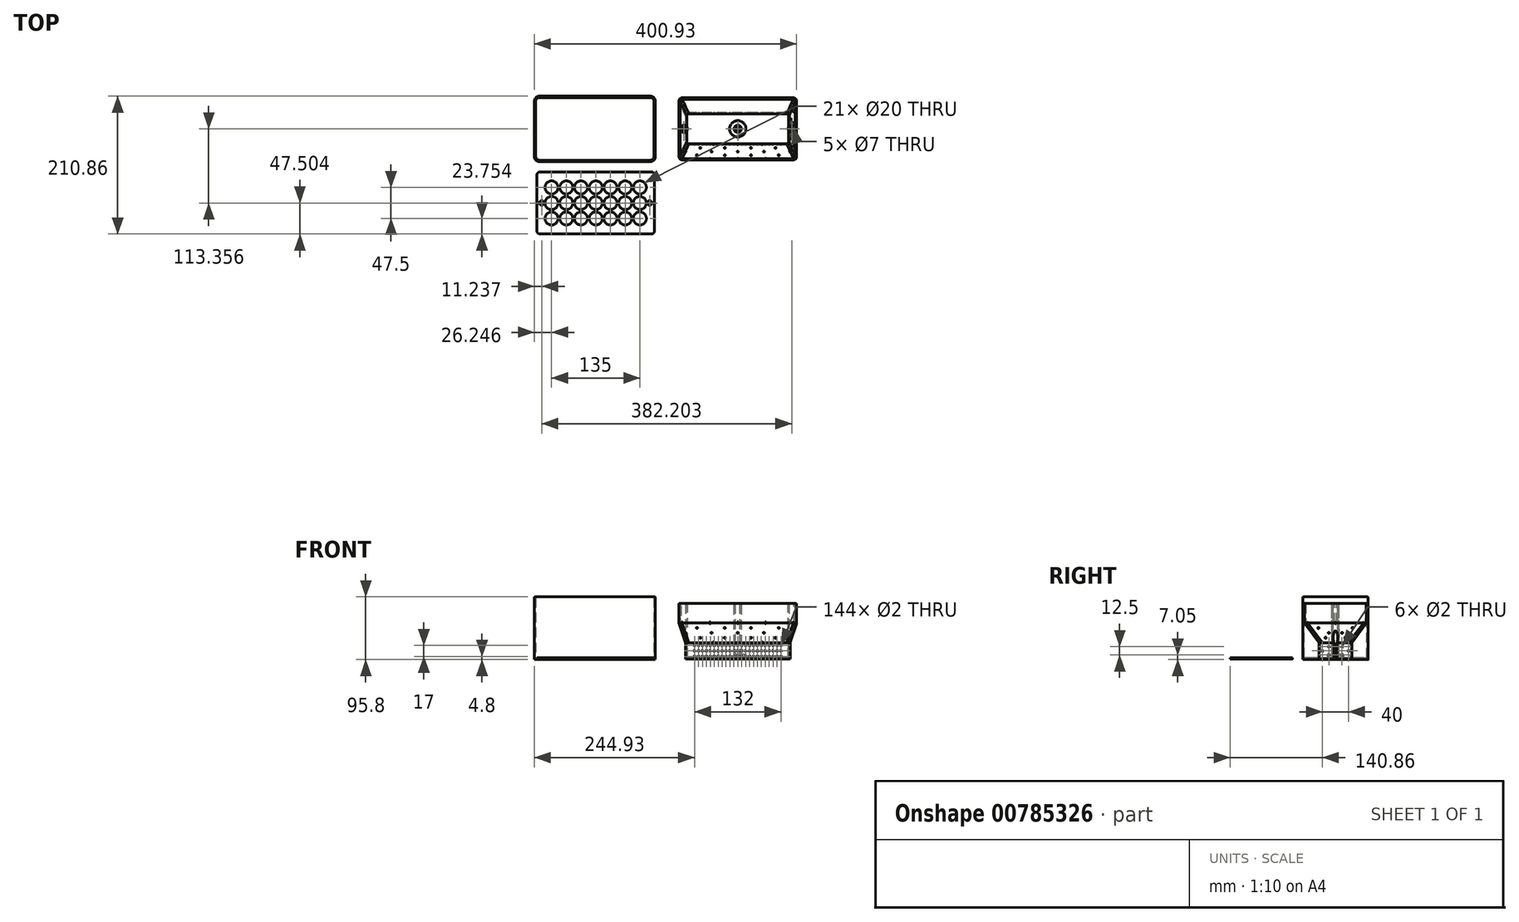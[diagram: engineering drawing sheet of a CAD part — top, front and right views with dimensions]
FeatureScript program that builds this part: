
annotation { "Feature Type Name" : "Feature", "Feature Type Description" : "" }
export const myFeature = defineFeature(function(context is Context, id is Id, definition is map)
    precondition{}
    {
        {
            var Q0;
            Q0=qCreatedBy(makeId("Top.planeOp"),FACE);
            var sketch = newSketch(context, id + "F0", { "sketchPlane" : qUnion([Q0])});
            skLineSegment(sketch, "E0.bottom", {"start": v(75, 25) * mm, "end": v(-75, 25) * mm});
            skLineSegment(sketch, "E0.top", {"start": v(75, -25) * mm, "end": v(-75, -25) * mm});
            skLineSegment(sketch, "E0.left", {"start": v(80, 20) * mm, "end": v(80, -20) * mm});
            skLineSegment(sketch, "E0.right", {"start": v(-80, 20) * mm, "end": v(-80, -20) * mm});
            skPoint(sketch, "E0.middle", {"position": v(0, 0) * mm});
            skPoint(sketch, "E1.visualSharp", {"position": v(-80, 25) * mm});
            skArc(sketch, "E1.filletArc", {"start": v(-75, 25) * mm, "mid": v(-78.54, 23.54) * mm, "end": v(-80, 20) * mm});
            skPoint(sketch, "E2.visualSharp", {"position": v(-80, -25) * mm});
            skArc(sketch, "E2.filletArc", {"start": v(-80, -20) * mm, "mid": v(-78.54, -23.54) * mm, "end": v(-75, -25) * mm});
            skPoint(sketch, "E3.visualSharp", {"position": v(80, -25) * mm});
            skArc(sketch, "E3.filletArc", {"start": v(75, -25) * mm, "mid": v(78.54, -23.54) * mm, "end": v(80, -20) * mm});
            skPoint(sketch, "E4.visualSharp", {"position": v(80, 25) * mm});
            skArc(sketch, "E4.filletArc", {"start": v(80, 20) * mm, "mid": v(78.54, 23.54) * mm, "end": v(75, 25) * mm});
            skSolve(sketch);
        }
        {
            var Q0;
            Q0 = qSketchRegion(id + "F0", true);
            extrude(context, id + "F1", {"entities" : qUnion([Q0]), "depth" : 25 * mm, "offsetDistance" : 25 * mm});
        }
        {
            var Q0;
            Q0=makeQuery(id+"F1.opExtrude","CAP_FACE",FACE,{"disambiguationData":[OSD([sQuery(id+"F0.wireOp",EDGE,"E0.bottom"),sQuery(id+"F0.wireOp",EDGE,"E0.top"),sQuery(id+"F0.wireOp",EDGE,"E0.left"),sQuery(id+"F0.wireOp",EDGE,"E0.right")])],"isStart":false});
            cPlane(context, id + "F2", {"entities" : qUnion([Q0]), "cplaneType" : CPlaneType.OFFSET, "offset" : 30 * mm, "width" : 150 * mm, "height" : 150 * mm});
        }
        {
            var Q0;
            Q0=qCreatedBy(id+"F2.planeOp",FACE);
            var sketch = newSketch(context, id + "F3", { "sketchPlane" : qUnion([Q0])});
            skLineSegment(sketch, "E5.bottom", {"start": v(85, 47.5) * mm, "end": v(-85, 47.5) * mm});
            skLineSegment(sketch, "E5.top", {"start": v(85, -47.5) * mm, "end": v(-85, -47.5) * mm});
            skLineSegment(sketch, "E5.left", {"start": v(90, 42.5) * mm, "end": v(90, -42.5) * mm});
            skLineSegment(sketch, "E5.right", {"start": v(-90, 42.5) * mm, "end": v(-90, -42.5) * mm});
            skPoint(sketch, "E5.middle", {"position": v(0, 0) * mm});
            skPoint(sketch, "E6.visualSharp", {"position": v(-90, 47.5) * mm});
            skArc(sketch, "E6.filletArc", {"start": v(-85, 47.5) * mm, "mid": v(-88.54, 46.04) * mm, "end": v(-90, 42.5) * mm});
            skPoint(sketch, "E7.visualSharp", {"position": v(-90, -47.5) * mm});
            skArc(sketch, "E7.filletArc", {"start": v(-90, -42.5) * mm, "mid": v(-88.54, -46.04) * mm, "end": v(-85, -47.5) * mm});
            skPoint(sketch, "E8.visualSharp", {"position": v(90, -47.5) * mm});
            skArc(sketch, "E8.filletArc", {"start": v(85, -47.5) * mm, "mid": v(88.54, -46.04) * mm, "end": v(90, -42.5) * mm});
            skPoint(sketch, "E9.visualSharp", {"position": v(90, 47.5) * mm});
            skArc(sketch, "E9.filletArc", {"start": v(90, 42.5) * mm, "mid": v(88.54, 46.04) * mm, "end": v(85, 47.5) * mm});
            skPoint(sketch, "E10", {"position": v(-82.5, 0) * mm});
            skPoint(sketch, "E11.MirrorP", {"position": v(82.5, 0) * mm});
            skSolve(sketch);
        }
        {
            var Q1;
            Q1=makeQuery(id+"F1.opExtrude","CAP_FACE",FACE,{"disambiguationData":[OSD([sQuery(id+"F0.wireOp",EDGE,"E0.bottom"),sQuery(id+"F0.wireOp",EDGE,"E0.top"),sQuery(id+"F0.wireOp",EDGE,"E0.left"),sQuery(id+"F0.wireOp",EDGE,"E0.right"),sQuery(id+"F0.wireOp",EDGE,"E1.filletArc"),sQuery(id+"F0.wireOp",EDGE,"E2.filletArc"),sQuery(id+"F0.wireOp",EDGE,"E3.filletArc"),sQuery(id+"F0.wireOp",EDGE,"E4.filletArc")])],"isStart":false});
            var Q2;
            Q2=makeQuery(id+"F3.imprint","IMPRINT",FACE,{"disambiguationData":[TD([[makeQuery(id+"F3.imprint","IMPRINT",EDGE,{"derivedFrom":sQuery(id+"F3.wireOp",EDGE,"E5.bottom")}),1.0]])]});
            loft(context, id + "F4", {"operationType" : NewBodyOperationType.ADD, "sheetProfilesArray" : [{ "sheetProfileEntities" : qUnion([Q1]) }, { "sheetProfileEntities" : qUnion([Q2]) }]});
        }
        {
            var Q0;
            Q0=makeQuery(id+"F3.imprint","IMPRINT",FACE,{"disambiguationData":[TD([[makeQuery(id+"F3.imprint","IMPRINT",EDGE,{"derivedFrom":sQuery(id+"F3.wireOp",EDGE,"E5.bottom")}),1.0]])]});
            extrude(context, id + "F5", {"entities" : qUnion([Q0]), "operationType" : NewBodyOperationType.ADD, "depth" : 30 * mm, "offsetDistance" : 25 * mm});
        }
        {
            var Q0;
            Q0=makeQuery(id+"F1.opExtrude","SWEPT_FACE",FACE,{"disambiguationData":[OSD([sQuery(id+"F0.wireOp",EDGE,"E0.top")])]});
            var sketch = newSketch(context, id + "F6", { "sketchPlane" : qUnion([Q0])});
            skPoint(sketch, "E12", {"position": v(-36, 12.5) * mm});
            skPoint(sketch, "E13", {"position": v(-36, 4) * mm});
            skPoint(sketch, "E14", {"position": v(-36, 21) * mm});
            skPoint(sketch, "E15", {"position": v(-30, 21) * mm});
            skPoint(sketch, "E16", {"position": v(-30, 12.5) * mm});
            skPoint(sketch, "E17", {"position": v(-30, 4) * mm});
            skPoint(sketch, "E18", {"position": v(-24, 4) * mm});
            skPoint(sketch, "E19", {"position": v(-24, 12.5) * mm});
            skPoint(sketch, "E20", {"position": v(-24, 21) * mm});
            skPoint(sketch, "E21", {"position": v(-18, 21) * mm});
            skPoint(sketch, "E22", {"position": v(-18, 12.5) * mm});
            skPoint(sketch, "E23", {"position": v(-18, 4) * mm});
            skPoint(sketch, "E24", {"position": v(-12, 4) * mm});
            skPoint(sketch, "E25", {"position": v(-12, 12.5) * mm});
            skPoint(sketch, "E26", {"position": v(-12, 21) * mm});
            skPoint(sketch, "E27", {"position": v(-6, 21) * mm});
            skPoint(sketch, "E28", {"position": v(-6, 12.5) * mm});
            skPoint(sketch, "E29", {"position": v(-6, 4) * mm});
            skPoint(sketch, "E30", {"position": v(-42, 21) * mm});
            skPoint(sketch, "E31", {"position": v(-42, 12.5) * mm});
            skPoint(sketch, "E32", {"position": v(-42, 4) * mm});
            skPoint(sketch, "E33", {"position": v(-48, 4) * mm});
            skPoint(sketch, "E34", {"position": v(-48, 12.5) * mm});
            skPoint(sketch, "E35", {"position": v(-48, 21) * mm});
            skPoint(sketch, "E36", {"position": v(-54, 21) * mm});
            skPoint(sketch, "E37", {"position": v(-54, 12.5) * mm});
            skPoint(sketch, "E38", {"position": v(-54, 4) * mm});
            skPoint(sketch, "E39", {"position": v(-60, 4) * mm});
            skPoint(sketch, "E40", {"position": v(-60, 12.5) * mm});
            skPoint(sketch, "E41", {"position": v(-60, 21) * mm});
            skPoint(sketch, "E42", {"position": v(-66, 4) * mm});
            skPoint(sketch, "E43", {"position": v(-66, 12.5) * mm});
            skPoint(sketch, "E44", {"position": v(-66, 21) * mm});
            skPoint(sketch, "E45.MirrorP", {"position": v(66, 21) * mm});
            skPoint(sketch, "E46.MirrorP", {"position": v(66, 12.5) * mm});
            skPoint(sketch, "E47.MirrorP", {"position": v(66, 4) * mm});
            skPoint(sketch, "E48.MirrorP", {"position": v(60, 4) * mm});
            skPoint(sketch, "E49.MirrorP", {"position": v(60, 12.5) * mm});
            skPoint(sketch, "E50.MirrorP", {"position": v(60, 21) * mm});
            skPoint(sketch, "E51.MirrorP", {"position": v(54, 21) * mm});
            skPoint(sketch, "E52.MirrorP", {"position": v(54, 12.5) * mm});
            skPoint(sketch, "E53.MirrorP", {"position": v(54, 4) * mm});
            skPoint(sketch, "E54.MirrorP", {"position": v(48, 4) * mm});
            skPoint(sketch, "E55.MirrorP", {"position": v(48, 12.5) * mm});
            skPoint(sketch, "E56.MirrorP", {"position": v(48, 21) * mm});
            skPoint(sketch, "E57.MirrorP", {"position": v(42, 21) * mm});
            skPoint(sketch, "E58.MirrorP", {"position": v(42, 12.5) * mm});
            skPoint(sketch, "E59.MirrorP", {"position": v(42, 4) * mm});
            skPoint(sketch, "E60.MirrorP", {"position": v(36, 4) * mm});
            skPoint(sketch, "E61.MirrorP", {"position": v(36, 12.5) * mm});
            skPoint(sketch, "E62.MirrorP", {"position": v(36, 21) * mm});
            skPoint(sketch, "E63.MirrorP", {"position": v(30, 21) * mm});
            skPoint(sketch, "E64.MirrorP", {"position": v(30, 12.5) * mm});
            skPoint(sketch, "E65.MirrorP", {"position": v(30, 4) * mm});
            skPoint(sketch, "E66.MirrorP", {"position": v(24, 4) * mm});
            skPoint(sketch, "E67.MirrorP", {"position": v(24, 12.5) * mm});
            skPoint(sketch, "E68.MirrorP", {"position": v(24, 21) * mm});
            skPoint(sketch, "E69.MirrorP", {"position": v(18, 21) * mm});
            skPoint(sketch, "E70.MirrorP", {"position": v(18, 12.5) * mm});
            skPoint(sketch, "E71.MirrorP", {"position": v(18, 4) * mm});
            skPoint(sketch, "E72.MirrorP", {"position": v(12, 4) * mm});
            skPoint(sketch, "E73.MirrorP", {"position": v(12, 12.5) * mm});
            skPoint(sketch, "E74.MirrorP", {"position": v(12, 21) * mm});
            skPoint(sketch, "E75.MirrorP", {"position": v(6, 21) * mm});
            skPoint(sketch, "E76.MirrorP", {"position": v(6, 12.5) * mm});
            skPoint(sketch, "E77.MirrorP", {"position": v(6, 4) * mm});
            skPoint(sketch, "E78", {"position": v(0, 4) * mm});
            skPoint(sketch, "E79", {"position": v(0, 12.5) * mm});
            skPoint(sketch, "E80", {"position": v(0, 21) * mm});
            skSolve(sketch);
        }
        {
            var Q0;
            Q0=makeQuery(id+"F5.opExtrude","CAP_FACE",FACE,{"disambiguationData":[OSD([sQuery(id+"F3.wireOp",EDGE,"E5.bottom"),sQuery(id+"F3.wireOp",EDGE,"E5.top"),sQuery(id+"F3.wireOp",EDGE,"E5.left"),sQuery(id+"F3.wireOp",EDGE,"E5.right"),sQuery(id+"F3.wireOp",EDGE,"E6.filletArc"),sQuery(id+"F3.wireOp",EDGE,"E7.filletArc"),sQuery(id+"F3.wireOp",EDGE,"E8.filletArc"),sQuery(id+"F3.wireOp",EDGE,"E9.filletArc")])],"isStart":false});
            var sketch = newSketch(context, id + "F7", { "sketchPlane" : qUnion([Q0])});
            skPoint(sketch, "E81", {"position": v(-82.5, 0) * mm});
            skPoint(sketch, "E82.MirrorP", {"position": v(82.5, 0) * mm});
            skPoint(sketch, "E83", {"position": v(-90, 0) * mm});
            skPoint(sketch, "E84", {"position": v(90, 0) * mm});
            skPoint(sketch, "E85", {"position": v(0, 47.5) * mm});
            skPoint(sketch, "E86", {"position": v(0, -47.5) * mm});
            skLineSegment(sketch, "E87", {"start": v(-90, 0) * mm, "end": v(90, 0) * mm});
            skLineSegment(sketch, "E88", {"start": v(0, 47.5) * mm, "end": v(0, -47.5) * mm});
            skPoint(sketch, "E89", {"position": v(0, 0) * mm});
            skPoint(sketch, "E90", {"position": v(-45, 0) * mm});
            skPoint(sketch, "E91", {"position": v(45, 0) * mm});
            skSolve(sketch);
        }
        {
            var Q0;
            Q0=sQuery(id+"F7.wireOp",VERTEX,"E81");
            var Q1;
            Q1=sQuery(id+"F7.wireOp",VERTEX,"E82.MirrorP");
            var Q2;
            Q2=makeQuery(id+"F1.opExtrude","SWEPT_BODY",BODY,{"disambiguationData":[OSD([sQuery(id+"F0.wireOp",EDGE,"E0.bottom"),sQuery(id+"F0.wireOp",EDGE,"E0.top"),sQuery(id+"F0.wireOp",EDGE,"E0.left"),sQuery(id+"F0.wireOp",EDGE,"E0.right"),sQuery(id+"F0.wireOp",EDGE,"E1.filletArc"),sQuery(id+"F0.wireOp",EDGE,"E2.filletArc"),sQuery(id+"F0.wireOp",EDGE,"E3.filletArc"),sQuery(id+"F0.wireOp",EDGE,"E4.filletArc")])]});
            hole(context, id + "F8", {"style" : HoleStyle.SIMPLE, "endStyle" : HoleEndStyle.THROUGH, "holeDiameter" : 7 * mm, "majorDiameter" : 5 * mm, "isTappedThrough" : true, "tappedDepth" : 12 * mm, "tapClearance" : 3, "locations" : qUnion([Q0, Q1]), "scope" : qUnion([Q2])});
        }
        {
            var Q0;
            Q0=sQuery(id+"F7.wireOp",VERTEX,"E89");
            var Q1;
            Q1=makeQuery(id+"F1.opExtrude","SWEPT_BODY",BODY,{"disambiguationData":[OSD([sQuery(id+"F0.wireOp",EDGE,"E0.bottom"),sQuery(id+"F0.wireOp",EDGE,"E0.top"),sQuery(id+"F0.wireOp",EDGE,"E0.left"),sQuery(id+"F0.wireOp",EDGE,"E0.right"),sQuery(id+"F0.wireOp",EDGE,"E1.filletArc"),sQuery(id+"F0.wireOp",EDGE,"E2.filletArc"),sQuery(id+"F0.wireOp",EDGE,"E3.filletArc"),sQuery(id+"F0.wireOp",EDGE,"E4.filletArc")])]});
            hole(context, id + "F9", {"style" : HoleStyle.SIMPLE, "endStyle" : HoleEndStyle.THROUGH, "holeDiameter" : 7 * mm, "majorDiameter" : 5 * mm, "isTappedThrough" : true, "tappedDepth" : 12 * mm, "tapClearance" : 3, "locations" : qUnion([Q0]), "scope" : qUnion([Q1])});
        }
        {
            var Q0;
            Q0=makeQuery(id+"F5.opExtrude","CAP_FACE",FACE,{"disambiguationData":[OSD([sQuery(id+"F3.wireOp",EDGE,"E5.bottom"),sQuery(id+"F3.wireOp",EDGE,"E5.top"),sQuery(id+"F3.wireOp",EDGE,"E5.left"),sQuery(id+"F3.wireOp",EDGE,"E5.right"),sQuery(id+"F3.wireOp",EDGE,"E6.filletArc"),sQuery(id+"F3.wireOp",EDGE,"E7.filletArc"),sQuery(id+"F3.wireOp",EDGE,"E8.filletArc"),sQuery(id+"F3.wireOp",EDGE,"E9.filletArc")])],"isStart":false});
            shell(context, id + "F10", {"entities" : qUnion([Q0]), "thickness" : 2.1 * mm});
        }
        {
            var Q0;
            Q0=sQuery(id+"F6.wireOp",VERTEX,"E44");
            var Q1;
            Q1=sQuery(id+"F6.wireOp",VERTEX,"E43");
            var Q2;
            Q2=sQuery(id+"F6.wireOp",VERTEX,"E42");
            var Q3;
            Q3=sQuery(id+"F6.wireOp",VERTEX,"E39");
            var Q4;
            Q4=sQuery(id+"F6.wireOp",VERTEX,"E40");
            var Q5;
            Q5=sQuery(id+"F6.wireOp",VERTEX,"E41");
            var Q6;
            Q6=sQuery(id+"F6.wireOp",VERTEX,"E36");
            var Q7;
            Q7=sQuery(id+"F6.wireOp",VERTEX,"E37");
            var Q8;
            Q8=sQuery(id+"F6.wireOp",VERTEX,"E38");
            var Q9;
            Q9=sQuery(id+"F6.wireOp",VERTEX,"E33");
            var Q10;
            Q10=sQuery(id+"F6.wireOp",VERTEX,"E34");
            var Q11;
            Q11=sQuery(id+"F6.wireOp",VERTEX,"E35");
            var Q12;
            Q12=sQuery(id+"F6.wireOp",VERTEX,"E30");
            var Q13;
            Q13=sQuery(id+"F6.wireOp",VERTEX,"E31");
            var Q14;
            Q14=sQuery(id+"F6.wireOp",VERTEX,"E32");
            var Q15;
            Q15=sQuery(id+"F6.wireOp",VERTEX,"E13");
            var Q16;
            Q16=sQuery(id+"F6.wireOp",VERTEX,"E12");
            var Q17;
            Q17=sQuery(id+"F6.wireOp",VERTEX,"E14");
            var Q18;
            Q18=sQuery(id+"F6.wireOp",VERTEX,"E15");
            var Q19;
            Q19=sQuery(id+"F6.wireOp",VERTEX,"E16");
            var Q20;
            Q20=sQuery(id+"F6.wireOp",VERTEX,"E17");
            var Q21;
            Q21=sQuery(id+"F6.wireOp",VERTEX,"E18");
            var Q22;
            Q22=sQuery(id+"F6.wireOp",VERTEX,"E19");
            var Q23;
            Q23=sQuery(id+"F6.wireOp",VERTEX,"E20");
            var Q24;
            Q24=sQuery(id+"F6.wireOp",VERTEX,"E21");
            var Q25;
            Q25=sQuery(id+"F6.wireOp",VERTEX,"E22");
            var Q26;
            Q26=sQuery(id+"F6.wireOp",VERTEX,"E23");
            var Q27;
            Q27=sQuery(id+"F6.wireOp",VERTEX,"E25");
            var Q28;
            Q28=sQuery(id+"F6.wireOp",VERTEX,"E24");
            var Q29;
            Q29=sQuery(id+"F6.wireOp",VERTEX,"E26");
            var Q30;
            Q30=sQuery(id+"F6.wireOp",VERTEX,"E27");
            var Q31;
            Q31=sQuery(id+"F6.wireOp",VERTEX,"E28");
            var Q32;
            Q32=sQuery(id+"F6.wireOp",VERTEX,"E29");
            var Q33;
            Q33=sQuery(id+"F6.wireOp",VERTEX,"E78");
            var Q34;
            Q34=sQuery(id+"F6.wireOp",VERTEX,"E79");
            var Q35;
            Q35=sQuery(id+"F6.wireOp",VERTEX,"E80");
            var Q36;
            Q36=sQuery(id+"F6.wireOp",VERTEX,"E75.MirrorP");
            var Q37;
            Q37=sQuery(id+"F6.wireOp",VERTEX,"E76.MirrorP");
            var Q38;
            Q38=sQuery(id+"F6.wireOp",VERTEX,"E77.MirrorP");
            var Q39;
            Q39=sQuery(id+"F6.wireOp",VERTEX,"E72.MirrorP");
            var Q40;
            Q40=sQuery(id+"F6.wireOp",VERTEX,"E73.MirrorP");
            var Q41;
            Q41=sQuery(id+"F6.wireOp",VERTEX,"E74.MirrorP");
            var Q42;
            Q42=sQuery(id+"F6.wireOp",VERTEX,"E70.MirrorP");
            var Q43;
            Q43=sQuery(id+"F6.wireOp",VERTEX,"E69.MirrorP");
            var Q44;
            Q44=sQuery(id+"F6.wireOp",VERTEX,"E71.MirrorP");
            var Q45;
            Q45=sQuery(id+"F6.wireOp",VERTEX,"E66.MirrorP");
            var Q46;
            Q46=sQuery(id+"F6.wireOp",VERTEX,"E67.MirrorP");
            var Q47;
            Q47=sQuery(id+"F6.wireOp",VERTEX,"E68.MirrorP");
            var Q48;
            Q48=sQuery(id+"F6.wireOp",VERTEX,"E63.MirrorP");
            var Q49;
            Q49=sQuery(id+"F6.wireOp",VERTEX,"E64.MirrorP");
            var Q50;
            Q50=sQuery(id+"F6.wireOp",VERTEX,"E65.MirrorP");
            var Q51;
            Q51=sQuery(id+"F6.wireOp",VERTEX,"E60.MirrorP");
            var Q52;
            Q52=sQuery(id+"F6.wireOp",VERTEX,"E61.MirrorP");
            var Q53;
            Q53=sQuery(id+"F6.wireOp",VERTEX,"E62.MirrorP");
            var Q54;
            Q54=sQuery(id+"F6.wireOp",VERTEX,"E57.MirrorP");
            var Q55;
            Q55=sQuery(id+"F6.wireOp",VERTEX,"E58.MirrorP");
            var Q56;
            Q56=sQuery(id+"F6.wireOp",VERTEX,"E59.MirrorP");
            var Q57;
            Q57=sQuery(id+"F6.wireOp",VERTEX,"E54.MirrorP");
            var Q58;
            Q58=sQuery(id+"F6.wireOp",VERTEX,"E55.MirrorP");
            var Q59;
            Q59=sQuery(id+"F6.wireOp",VERTEX,"E56.MirrorP");
            var Q60;
            Q60=sQuery(id+"F6.wireOp",VERTEX,"E51.MirrorP");
            var Q61;
            Q61=sQuery(id+"F6.wireOp",VERTEX,"E53.MirrorP");
            var Q62;
            Q62=sQuery(id+"F6.wireOp",VERTEX,"E52.MirrorP");
            var Q63;
            Q63=sQuery(id+"F6.wireOp",VERTEX,"E50.MirrorP");
            var Q64;
            Q64=sQuery(id+"F6.wireOp",VERTEX,"E49.MirrorP");
            var Q65;
            Q65=sQuery(id+"F6.wireOp",VERTEX,"E48.MirrorP");
            var Q66;
            Q66=sQuery(id+"F6.wireOp",VERTEX,"E45.MirrorP");
            var Q67;
            Q67=sQuery(id+"F6.wireOp",VERTEX,"E46.MirrorP");
            var Q68;
            Q68=sQuery(id+"F6.wireOp",VERTEX,"E47.MirrorP");
            var Q69;
            Q69=sQuery(id+"F6.wireOp",VERTEX,"2dc27312-36e5-447e-a7eb-3d5d8e6497cb");
            var Q70;
            Q70=makeQuery(id+"F1.opExtrude","SWEPT_BODY",BODY,{"disambiguationData":[OSD([sQuery(id+"F0.wireOp",EDGE,"E0.bottom"),sQuery(id+"F0.wireOp",EDGE,"E0.top"),sQuery(id+"F0.wireOp",EDGE,"E0.left"),sQuery(id+"F0.wireOp",EDGE,"E0.right"),sQuery(id+"F0.wireOp",EDGE,"E1.filletArc"),sQuery(id+"F0.wireOp",EDGE,"E2.filletArc"),sQuery(id+"F0.wireOp",EDGE,"E3.filletArc"),sQuery(id+"F0.wireOp",EDGE,"E4.filletArc")])]});
            hole(context, id + "F11", {"style" : HoleStyle.SIMPLE, "endStyle" : HoleEndStyle.THROUGH, "holeDiameter" : 2 * mm, "majorDiameter" : 5 * mm, "isTappedThrough" : true, "tappedDepth" : 12 * mm, "tapClearance" : 3, "locations" : qUnion([Q0, Q1, Q2, Q3, Q4, Q5, Q6, Q7, Q8, Q9, Q10, Q11, Q12, Q13, Q14, Q15, Q16, Q17, Q18, Q19, Q20, Q21, Q22, Q23, Q24, Q25, Q26, Q27, Q28, Q29, Q30, Q31, Q32, Q33, Q34, Q35, Q36, Q37, Q38, Q39, Q40, Q41, Q42, Q43, Q44, Q45, Q46, Q47, Q48, Q49, Q50, Q51, Q52, Q53, Q54, Q55, Q56, Q57, Q58, Q59, Q60, Q61, Q62, Q63, Q64, Q65, Q66, Q67, Q68, Q69]), "scope" : qUnion([Q70])});
        }
        {
            var Q0;
            Q0=makeQuery(id+"F4.opLoft","SWEPT_FACE",FACE,{"disambiguationData":[OSD([sQuery(id+"F0.wireOp",EDGE,"E0.top"),sQuery(id+"F0.wireOp",EDGE,"E2.filletArc"),sQuery(id+"F0.wireOp",EDGE,"E3.filletArc"),sQuery(id+"F3.wireOp",EDGE,"E5.top"),sQuery(id+"F3.wireOp",EDGE,"E7.filletArc"),sQuery(id+"F3.wireOp",EDGE,"E8.filletArc")])]});
            var sketch = newSketch(context, id + "F12", { "sketchPlane" : qUnion([Q0])});
            skPoint(sketch, "E92", {"position": v(0, 35) * mm});
            skPoint(sketch, "E93", {"position": v(0, 72.5) * mm});
            skPoint(sketch, "E94", {"position": v(-75, 35) * mm});
            skPoint(sketch, "E95", {"position": v(75, 35) * mm});
            skPoint(sketch, "E96", {"position": v(85, 72.5) * mm});
            skPoint(sketch, "E97", {"position": v(-85, 72.5) * mm});
            skPoint(sketch, "E98", {"position": v(0, 53.75) * mm});
            skPoint(sketch, "E99", {"position": v(-37.5, 35) * mm});
            skPoint(sketch, "E100", {"position": v(-42.5, 72.5) * mm});
            skPoint(sketch, "E101", {"position": v(42.5, 72.5) * mm});
            skPoint(sketch, "E102", {"position": v(37.5, 35) * mm});
            skPoint(sketch, "E103", {"position": v(-80, 53.75) * mm});
            skPoint(sketch, "E104", {"position": v(80, 53.75) * mm});
            skPoint(sketch, "E105", {"position": v(-40, 53.75) * mm});
            skPoint(sketch, "E106", {"position": v(40, 53.75) * mm});
            skPoint(sketch, "E107", {"position": v(-57.5, 44.38) * mm});
            skPoint(sketch, "E108", {"position": v(-62.5, 63.12) * mm});
            skPoint(sketch, "E109", {"position": v(-20, 63.12) * mm});
            skPoint(sketch, "E110", {"position": v(-20, 44.37) * mm});
            skPoint(sketch, "E111", {"position": v(20, 44.38) * mm});
            skPoint(sketch, "E112", {"position": v(20, 63.12) * mm});
            skPoint(sketch, "E113", {"position": v(62.5, 63.12) * mm});
            skPoint(sketch, "E114", {"position": v(57.5, 44.38) * mm});
            skSolve(sketch);
        }
        {
            var Q0;
            Q0=sQuery(id+"F12.wireOp",VERTEX,"E97");
            var Q1;
            Q1=sQuery(id+"F12.wireOp",VERTEX,"E103");
            var Q2;
            Q2=sQuery(id+"F12.wireOp",VERTEX,"E94");
            var Q3;
            Q3=sQuery(id+"F12.wireOp",VERTEX,"E107");
            var Q4;
            Q4=sQuery(id+"F12.wireOp",VERTEX,"E105");
            var Q5;
            Q5=sQuery(id+"F12.wireOp",VERTEX,"E109");
            var Q6;
            Q6=sQuery(id+"F12.wireOp",VERTEX,"E93");
            var Q7;
            Q7=sQuery(id+"F12.wireOp",VERTEX,"E100");
            var Q8;
            Q8=sQuery(id+"F12.wireOp",VERTEX,"E99");
            var Q9;
            Q9=sQuery(id+"F12.wireOp",VERTEX,"E110");
            var Q10;
            Q10=sQuery(id+"F12.wireOp",VERTEX,"E98");
            var Q11;
            Q11=sQuery(id+"F12.wireOp",VERTEX,"E92");
            var Q12;
            Q12=sQuery(id+"F12.wireOp",VERTEX,"E111");
            var Q13;
            Q13=sQuery(id+"F12.wireOp",VERTEX,"E106");
            var Q14;
            Q14=sQuery(id+"F12.wireOp",VERTEX,"E113");
            var Q15;
            Q15=sQuery(id+"F12.wireOp",VERTEX,"E96");
            var Q16;
            Q16=sQuery(id+"F12.wireOp",VERTEX,"E104");
            var Q17;
            Q17=sQuery(id+"F12.wireOp",VERTEX,"E101");
            var Q18;
            Q18=sQuery(id+"F12.wireOp",VERTEX,"E112");
            var Q19;
            Q19=sQuery(id+"F12.wireOp",VERTEX,"E114");
            var Q20;
            Q20=sQuery(id+"F12.wireOp",VERTEX,"E95");
            var Q21;
            Q21=sQuery(id+"F12.wireOp",VERTEX,"E102");
            var Q22;
            Q22=sQuery(id+"F12.wireOp",VERTEX,"E108");
            var Q23;
            Q23=makeQuery(id+"F1.opExtrude","SWEPT_BODY",BODY,{"disambiguationData":[OSD([sQuery(id+"F0.wireOp",EDGE,"E0.bottom"),sQuery(id+"F0.wireOp",EDGE,"E0.top"),sQuery(id+"F0.wireOp",EDGE,"E0.left"),sQuery(id+"F0.wireOp",EDGE,"E0.right"),sQuery(id+"F0.wireOp",EDGE,"E1.filletArc"),sQuery(id+"F0.wireOp",EDGE,"E2.filletArc"),sQuery(id+"F0.wireOp",EDGE,"E3.filletArc"),sQuery(id+"F0.wireOp",EDGE,"E4.filletArc")])]});
            hole(context, id + "F13", {"style" : HoleStyle.SIMPLE, "endStyle" : HoleEndStyle.BLIND, "holeDiameter" : 2 * mm, "majorDiameter" : 5 * mm, "holeDepth" : 4 * mm, "isTappedThrough" : true, "tappedDepth" : 12 * mm, "tapClearance" : 3, "locations" : qUnion([Q0, Q1, Q2, Q3, Q4, Q5, Q6, Q7, Q8, Q9, Q10, Q11, Q12, Q13, Q14, Q15, Q16, Q17, Q18, Q19, Q20, Q21, Q22]), "scope" : qUnion([Q23])});
        }
        {
            var Q0;
            Q0=makeQuery(id+"F4.opLoft","SWEPT_FACE",FACE,{"disambiguationData":[OSD([sQuery(id+"F0.wireOp",EDGE,"E0.left"),sQuery(id+"F0.wireOp",EDGE,"E3.filletArc"),sQuery(id+"F0.wireOp",EDGE,"E4.filletArc"),sQuery(id+"F3.wireOp",EDGE,"E5.left"),sQuery(id+"F3.wireOp",EDGE,"E8.filletArc"),sQuery(id+"F3.wireOp",EDGE,"E9.filletArc")])]});
            var sketch = newSketch(context, id + "F14", { "sketchPlane" : qUnion([Q0])});
            skPoint(sketch, "E115", {"position": v(-42.5, 80.64) * mm});
            skPoint(sketch, "E116", {"position": v(42.5, 80.64) * mm});
            skPoint(sketch, "E117", {"position": v(20, 49.02) * mm});
            skPoint(sketch, "E118", {"position": v(-20, 49.02) * mm});
            skPoint(sketch, "E119", {"position": v(0, 80.64) * mm});
            skPoint(sketch, "E120", {"position": v(-10, 64.83) * mm});
            skPoint(sketch, "E121", {"position": v(10, 64.83) * mm});
            skPoint(sketch, "E122", {"position": v(-26.25, 72.73) * mm});
            skPoint(sketch, "E123", {"position": v(26.25, 72.73) * mm});
            skPoint(sketch, "E124", {"position": v(15, 56.92) * mm});
            skPoint(sketch, "E125", {"position": v(-15, 56.92) * mm});
            skSolve(sketch);
        }
        {
            var Q0;
            {var subQ3=sQuery(id+"F0.wireOp",EDGE,"E3.filletArc");var subQ4=sQuery(id+"F0.wireOp",EDGE,"E0.left");Q0=makeQuery(id+"F8.hole-1.boolean.opBoolean","SPLIT",FACE,{"disambiguationData":[TD([makeQuery(id+"F1.opExtrude","SWEPT_FACE",FACE,{"disambiguationData":[OSD([subQ3])]})])],"derivedFrom":makeQuery(id+"F1.opExtrude","SWEPT_FACE",FACE,{"disambiguationData":[OSD([subQ4])]})});}
            var sketch = newSketch(context, id + "F15", { "sketchPlane" : qUnion([Q0])});
            skPoint(sketch, "E126", {"position": v(-20, 0) * mm});
            skPoint(sketch, "E127", {"position": v(20, 0) * mm});
            skPoint(sketch, "E128", {"position": v(-20, 12.5) * mm});
            skPoint(sketch, "E129", {"position": v(20, 12.5) * mm});
            skPoint(sketch, "E130", {"position": v(0, 12.5) * mm});
            skPoint(sketch, "E131", {"position": v(-10, 6.25) * mm});
            skPoint(sketch, "E132", {"position": v(-10, 18.75) * mm});
            skPoint(sketch, "E133", {"position": v(10, 18.75) * mm});
            skPoint(sketch, "E134", {"position": v(10, 6.25) * mm});
            skSolve(sketch);
        }
        {
            var Q0;
            Q0=sQuery(id+"F14.wireOp",VERTEX,"E115");
            var Q1;
            Q1=sQuery(id+"F14.wireOp",VERTEX,"E122");
            var Q2;
            Q2=sQuery(id+"F14.wireOp",VERTEX,"E118");
            var Q3;
            Q3=sQuery(id+"F14.wireOp",VERTEX,"E125");
            var Q4;
            Q4=sQuery(id+"F14.wireOp",VERTEX,"E120");
            var Q5;
            Q5=sQuery(id+"F14.wireOp",VERTEX,"E119");
            var Q6;
            Q6=sQuery(id+"F14.wireOp",VERTEX,"E121");
            var Q7;
            Q7=sQuery(id+"F14.wireOp",VERTEX,"E124");
            var Q8;
            Q8=sQuery(id+"F14.wireOp",VERTEX,"E117");
            var Q9;
            Q9=sQuery(id+"F14.wireOp",VERTEX,"E123");
            var Q10;
            Q10=sQuery(id+"F14.wireOp",VERTEX,"E116");
            var Q11;
            Q11=sQuery(id+"F15.wireOp",VERTEX,"E128");
            var Q12;
            Q12=sQuery(id+"F15.wireOp",VERTEX,"E131");
            var Q13;
            Q13=sQuery(id+"F15.wireOp",VERTEX,"E132");
            var Q14;
            Q14=sQuery(id+"F15.wireOp",VERTEX,"E133");
            var Q15;
            Q15=sQuery(id+"F15.wireOp",VERTEX,"E134");
            var Q16;
            Q16=sQuery(id+"F15.wireOp",VERTEX,"E129");
            var Q17;
            Q17=makeQuery(id+"F1.opExtrude","SWEPT_BODY",BODY,{"disambiguationData":[OSD([sQuery(id+"F0.wireOp",EDGE,"E0.bottom"),sQuery(id+"F0.wireOp",EDGE,"E0.top"),sQuery(id+"F0.wireOp",EDGE,"E0.left"),sQuery(id+"F0.wireOp",EDGE,"E0.right"),sQuery(id+"F0.wireOp",EDGE,"E1.filletArc"),sQuery(id+"F0.wireOp",EDGE,"E2.filletArc"),sQuery(id+"F0.wireOp",EDGE,"E3.filletArc"),sQuery(id+"F0.wireOp",EDGE,"E4.filletArc")])]});
            hole(context, id + "F16", {"style" : HoleStyle.SIMPLE, "endStyle" : HoleEndStyle.BLIND, "holeDiameter" : 2 * mm, "majorDiameter" : 5 * mm, "holeDepth" : 4 * mm, "isTappedThrough" : true, "tappedDepth" : 12 * mm, "tapClearance" : 3, "locations" : qUnion([Q0, Q1, Q2, Q3, Q4, Q5, Q6, Q7, Q8, Q9, Q10, Q11, Q12, Q13, Q14, Q15, Q16]), "scope" : qUnion([Q17])});
        }
        {
            var Q0;
            Q0=makeQuery(id+"F10.opShell","OFFSET_FACE",FACE,{"disambiguationData":[OSD([sQuery(id+"F0.wireOp",EDGE,"E0.bottom"),sQuery(id+"F0.wireOp",EDGE,"E0.top"),sQuery(id+"F0.wireOp",EDGE,"E0.left"),sQuery(id+"F0.wireOp",EDGE,"E0.right"),sQuery(id+"F0.wireOp",EDGE,"E1.filletArc"),sQuery(id+"F0.wireOp",EDGE,"E2.filletArc"),sQuery(id+"F0.wireOp",EDGE,"E3.filletArc"),sQuery(id+"F0.wireOp",EDGE,"E4.filletArc")])]});
            var sketch = newSketch(context, id + "F17", { "sketchPlane" : qUnion([Q0])});
            skCircle(sketch, "E135", {"center": v(0, 0) * mm, "radius": 12.5 * mm});
            skCircle(sketch, "E136", {"center": v(0, 0) * mm, "radius": 4.45 * mm});
            skSolve(sketch);
        }
        {
            var Q0;
            Q0=makeQuery(id+"F17.imprint","IMPRINT",FACE,{"disambiguationData":[TD([[makeQuery(id+"F17.imprint","IMPRINT",EDGE,{"derivedFrom":sQuery(id+"F17.wireOp",EDGE,"E135")}),1.0]])]});
            extrude(context, id + "F18", {"entities" : qUnion([Q0]), "operationType" : NewBodyOperationType.ADD, "depth" : 5 * mm, "offsetDistance" : 25 * mm});
        }
        {
            var Q0;
            Q0=qCreatedBy(makeId("Top.planeOp"),FACE);
            var sketch = newSketch(context, id + "F19", { "sketchPlane" : qUnion([Q0])});
            skLineSegment(sketch, "E137", {"start": v(-308.43, 0) * mm, "end": v(-128.43, 0) * mm});
            skPoint(sketch, "E138", {"position": v(-218.43, 0) * mm});
            skLineSegment(sketch, "E139", {"start": v(-218.43, 47.5) * mm, "end": v(-218.43, -47.5) * mm});
            skLineSegment(sketch, "E140.bottom", {"start": v(-303.43, 47.5) * mm, "end": v(-133.43, 47.5) * mm});
            skLineSegment(sketch, "E140.top", {"start": v(-303.43, -47.5) * mm, "end": v(-133.43, -47.5) * mm});
            skLineSegment(sketch, "E140.left", {"start": v(-308.43, 42.5) * mm, "end": v(-308.43, -42.5) * mm});
            skLineSegment(sketch, "E140.right", {"start": v(-128.43, 42.5) * mm, "end": v(-128.43, -42.5) * mm});
            skPoint(sketch, "E141.visualSharp", {"position": v(-308.43, 47.5) * mm});
            skArc(sketch, "E141.filletArc", {"start": v(-303.43, 47.5) * mm, "mid": v(-306.97, 46.04) * mm, "end": v(-308.43, 42.5) * mm});
            skPoint(sketch, "E142.visualSharp", {"position": v(-308.43, -47.5) * mm});
            skArc(sketch, "E142.filletArc", {"start": v(-308.43, -42.5) * mm, "mid": v(-306.97, -46.04) * mm, "end": v(-303.43, -47.5) * mm});
            skPoint(sketch, "E143.visualSharp", {"position": v(-128.43, -47.5) * mm});
            skArc(sketch, "E143.filletArc", {"start": v(-133.43, -47.5) * mm, "mid": v(-129.9, -46.04) * mm, "end": v(-128.43, -42.5) * mm});
            skPoint(sketch, "E144.visualSharp", {"position": v(-128.43, 47.5) * mm});
            skArc(sketch, "E144.filletArc", {"start": v(-128.43, 42.5) * mm, "mid": v(-129.9, 46.04) * mm, "end": v(-133.43, 47.5) * mm});
            skArc(sketch, "E145.0", {"start": v(-310.93, -42.5) * mm, "mid": v(-308.73, -47.8) * mm, "end": v(-303.43, -50) * mm});
            skLineSegment(sketch, "E145.1", {"start": v(-310.93, 42.5) * mm, "end": v(-310.93, -42.5) * mm});
            skLineSegment(sketch, "E145.2", {"start": v(-303.43, -50) * mm, "end": v(-133.43, -50) * mm});
            skArc(sketch, "E145.3", {"start": v(-303.43, 50) * mm, "mid": v(-308.73, 47.8) * mm, "end": v(-310.93, 42.5) * mm});
            skArc(sketch, "E145.4", {"start": v(-133.43, -50) * mm, "mid": v(-128.13, -47.8) * mm, "end": v(-125.93, -42.5) * mm});
            skLineSegment(sketch, "E145.5", {"start": v(-125.93, 42.5) * mm, "end": v(-125.93, -42.5) * mm});
            skArc(sketch, "E145.6", {"start": v(-125.93, 42.5) * mm, "mid": v(-128.13, 47.8) * mm, "end": v(-133.43, 50) * mm});
            skLineSegment(sketch, "E145.7", {"start": v(-303.43, 50) * mm, "end": v(-133.43, 50) * mm});
            skSolve(sketch);
        }
        {
            var Q0;
            Q0 = qSketchRegion(id + "F19", true);
            var Q1;
            {var subQ3=sQuery(id+"F19.wireOp",EDGE,"E141.filletArc");Q1=makeQuery(id+"F19.imprint","IMPRINT",FACE,{"disambiguationData":[TD([[makeQuery(id+"F19.imprint","IMPRINT",EDGE,{"derivedFrom":subQ3}),1.0]])]});}
            var Q2;
            {var subQ3=sQuery(id+"F19.wireOp",EDGE,"E144.filletArc");Q2=makeQuery(id+"F19.imprint","IMPRINT",FACE,{"disambiguationData":[TD([[makeQuery(id+"F19.imprint","IMPRINT",EDGE,{"derivedFrom":subQ3}),1.0]])]});}
            var Q3;
            {var subQ3=sQuery(id+"F19.wireOp",EDGE,"E142.filletArc");Q3=makeQuery(id+"F19.imprint","IMPRINT",FACE,{"disambiguationData":[TD([[makeQuery(id+"F19.imprint","IMPRINT",EDGE,{"derivedFrom":subQ3}),1.0]])]});}
            var Q4;
            {var subQ3=sQuery(id+"F19.wireOp",EDGE,"E143.filletArc");Q4=makeQuery(id+"F19.imprint","IMPRINT",FACE,{"disambiguationData":[TD([[makeQuery(id+"F19.imprint","IMPRINT",EDGE,{"derivedFrom":subQ3}),1.0]])]});}
            extrude(context, id + "F20", {"entities" : qUnion([Q0, Q1, Q2, Q3, Q4]), "depth" : 95 * mm, "offsetDistance" : 25 * mm});
        }
        {
            var Q0;
            Q0=makeQuery(id+"F20.opExtrude","CAP_FACE",FACE,{"disambiguationData":[OSD([sQuery(id+"F19.wireOp",EDGE,"E145.0"),sQuery(id+"F19.wireOp",EDGE,"E145.1"),sQuery(id+"F19.wireOp",EDGE,"E145.2"),sQuery(id+"F19.wireOp",EDGE,"E145.3"),sQuery(id+"F19.wireOp",EDGE,"E145.4"),sQuery(id+"F19.wireOp",EDGE,"E145.5"),sQuery(id+"F19.wireOp",EDGE,"E145.6"),sQuery(id+"F19.wireOp",EDGE,"E145.7")])],"isStart":false});
            shell(context, id + "F21", {"entities" : qUnion([Q0]), "thickness" : 2.1 * mm});
        }
        {
            var Q0;
            Q0=makeQuery(id+"F20.opExtrude","CAP_EDGE",EDGE,{"disambiguationData":[OSD([sQuery(id+"F19.wireOp",EDGE,"E145.7")])],"isStart":false});
            var Q1;
            {var subQ0=sQuery(id+"F19.wireOp",EDGE,"E145.7");Q1=makeQuery(id+"F21.opShell","OFFSET_EDGE",EDGE,{"disambiguationData":[OSD([subQ0]),TDD([makeQuery(id+"F20.opExtrude","CAP_EDGE",EDGE,{"disambiguationData":[OSD([subQ0])],"isStart":false})])]});}
            var Q2;
            Q2=makeQuery(id+"F20.opExtrude","CAP_EDGE",EDGE,{"disambiguationData":[OSD([sQuery(id+"F19.wireOp",EDGE,"E145.3")])],"isStart":false});
            var Q3;
            {var subQ0=sQuery(id+"F19.wireOp",EDGE,"E145.3");Q3=makeQuery(id+"F21.opShell","OFFSET_EDGE",EDGE,{"disambiguationData":[OSD([subQ0]),TDD([makeQuery(id+"F20.opExtrude","CAP_EDGE",EDGE,{"disambiguationData":[OSD([subQ0])],"isStart":false})])]});}
            var Q4;
            {var subQ0=sQuery(id+"F19.wireOp",EDGE,"E145.1");Q4=makeQuery(id+"F21.opShell","OFFSET_EDGE",EDGE,{"disambiguationData":[OSD([subQ0]),TDD([makeQuery(id+"F20.opExtrude","CAP_EDGE",EDGE,{"disambiguationData":[OSD([subQ0])],"isStart":false})])]});}
            var Q5;
            Q5=makeQuery(id+"F20.opExtrude","CAP_EDGE",EDGE,{"disambiguationData":[OSD([sQuery(id+"F19.wireOp",EDGE,"E145.1")])],"isStart":false});
            var Q6;
            Q6=makeQuery(id+"F20.opExtrude","CAP_EDGE",EDGE,{"disambiguationData":[OSD([sQuery(id+"F19.wireOp",EDGE,"E145.0")])],"isStart":false});
            var Q7;
            {var subQ0=sQuery(id+"F19.wireOp",EDGE,"E145.0");Q7=makeQuery(id+"F21.opShell","OFFSET_EDGE",EDGE,{"disambiguationData":[OSD([subQ0]),TDD([makeQuery(id+"F20.opExtrude","CAP_EDGE",EDGE,{"disambiguationData":[OSD([subQ0])],"isStart":false})])]});}
            var Q8;
            {var subQ0=sQuery(id+"F19.wireOp",EDGE,"E145.2");Q8=makeQuery(id+"F21.opShell","OFFSET_EDGE",EDGE,{"disambiguationData":[OSD([subQ0]),TDD([makeQuery(id+"F20.opExtrude","CAP_EDGE",EDGE,{"disambiguationData":[OSD([subQ0])],"isStart":false})])]});}
            var Q9;
            Q9=makeQuery(id+"F20.opExtrude","CAP_EDGE",EDGE,{"disambiguationData":[OSD([sQuery(id+"F19.wireOp",EDGE,"E145.2")])],"isStart":false});
            var Q10;
            {var subQ0=sQuery(id+"F19.wireOp",EDGE,"E145.4");Q10=makeQuery(id+"F21.opShell","OFFSET_EDGE",EDGE,{"disambiguationData":[OSD([subQ0]),TDD([makeQuery(id+"F20.opExtrude","CAP_EDGE",EDGE,{"disambiguationData":[OSD([subQ0])],"isStart":false})])]});}
            var Q11;
            Q11=makeQuery(id+"F20.opExtrude","CAP_EDGE",EDGE,{"disambiguationData":[OSD([sQuery(id+"F19.wireOp",EDGE,"E145.4")])],"isStart":false});
            var Q12;
            Q12=makeQuery(id+"F20.opExtrude","CAP_EDGE",EDGE,{"disambiguationData":[OSD([sQuery(id+"F19.wireOp",EDGE,"E145.5")])],"isStart":false});
            var Q13;
            {var subQ0=sQuery(id+"F19.wireOp",EDGE,"E145.5");Q13=makeQuery(id+"F21.opShell","OFFSET_EDGE",EDGE,{"disambiguationData":[OSD([subQ0]),TDD([makeQuery(id+"F20.opExtrude","CAP_EDGE",EDGE,{"disambiguationData":[OSD([subQ0])],"isStart":false})])]});}
            var Q14;
            {var subQ0=sQuery(id+"F19.wireOp",EDGE,"E145.6");Q14=makeQuery(id+"F21.opShell","OFFSET_EDGE",EDGE,{"disambiguationData":[OSD([subQ0]),TDD([makeQuery(id+"F20.opExtrude","CAP_EDGE",EDGE,{"disambiguationData":[OSD([subQ0])],"isStart":false})])]});}
            var Q15;
            Q15=makeQuery(id+"F20.opExtrude","CAP_EDGE",EDGE,{"disambiguationData":[OSD([sQuery(id+"F19.wireOp",EDGE,"E145.6")])],"isStart":false});
            fillet(context, id + "F22", {"entities" : qUnion([Q0, Q1, Q2, Q3, Q4, Q5, Q6, Q7, Q8, Q9, Q10, Q11, Q12, Q13, Q14, Q15]), "radius" : 1 * mm, "tangentPropagation" : true, "allowEdgeOverflow" : false});
        }
        {
            var Q0;
            Q0=makeQuery(id+"F20.opExtrude","CAP_FACE",FACE,{"disambiguationData":[OSD([sQuery(id+"F19.wireOp",EDGE,"E145.0"),sQuery(id+"F19.wireOp",EDGE,"E145.1"),sQuery(id+"F19.wireOp",EDGE,"E145.2"),sQuery(id+"F19.wireOp",EDGE,"E145.3"),sQuery(id+"F19.wireOp",EDGE,"E145.4"),sQuery(id+"F19.wireOp",EDGE,"E145.5"),sQuery(id+"F19.wireOp",EDGE,"E145.6"),sQuery(id+"F19.wireOp",EDGE,"E145.7")])],"isStart":true});
            extrude(context, id + "F23", {"entities" : qUnion([Q0]), "operationType" : NewBodyOperationType.ADD, "depth" : 0.8 * mm, "offsetDistance" : 25 * mm});
        }
        {
            var Q0;
            Q0=qCreatedBy(makeId("Top.planeOp"),FACE);
            var sketch = newSketch(context, id + "F24", { "sketchPlane" : qUnion([Q0])});
            skPoint(sketch, "E146", {"position": v(-217.18, -113.36) * mm});
            skLineSegment(sketch, "E147.bottom", {"start": v(-302.18, -65.86) * mm, "end": v(-132.18, -65.86) * mm});
            skLineSegment(sketch, "E147.top", {"start": v(-302.18, -160.86) * mm, "end": v(-132.18, -160.86) * mm});
            skLineSegment(sketch, "E147.left", {"start": v(-307.18, -70.86) * mm, "end": v(-307.18, -155.86) * mm});
            skLineSegment(sketch, "E147.right", {"start": v(-127.18, -70.86) * mm, "end": v(-127.18, -155.86) * mm});
            skPoint(sketch, "E148.visualSharp", {"position": v(-307.18, -65.86) * mm});
            skArc(sketch, "E148.filletArc", {"start": v(-302.18, -65.86) * mm, "mid": v(-305.72, -67.32) * mm, "end": v(-307.18, -70.86) * mm});
            skPoint(sketch, "E149.visualSharp", {"position": v(-307.18, -160.86) * mm});
            skArc(sketch, "E149.filletArc", {"start": v(-307.18, -155.86) * mm, "mid": v(-305.72, -159.4) * mm, "end": v(-302.18, -160.86) * mm});
            skPoint(sketch, "E150.visualSharp", {"position": v(-127.18, -160.86) * mm});
            skArc(sketch, "E150.filletArc", {"start": v(-132.18, -160.86) * mm, "mid": v(-128.65, -159.4) * mm, "end": v(-127.18, -155.86) * mm});
            skPoint(sketch, "E151.visualSharp", {"position": v(-127.18, -65.86) * mm});
            skArc(sketch, "E151.filletArc", {"start": v(-127.18, -70.86) * mm, "mid": v(-128.65, -67.32) * mm, "end": v(-132.18, -65.86) * mm});
            skPoint(sketch, "E152", {"position": v(-307.18, -113.36) * mm});
            skPoint(sketch, "E153", {"position": v(-127.18, -113.36) * mm});
            skPoint(sketch, "E154", {"position": v(-299.7, -113.36) * mm});
            skCircle(sketch, "E155", {"center": v(-299.7, -113.36) * mm, "radius": 3.5 * mm});
            skPoint(sketch, "E156", {"position": v(-134.68, -113.36) * mm});
            skCircle(sketch, "E157", {"center": v(-134.68, -113.36) * mm, "radius": 3.5 * mm});
            skPoint(sketch, "E158", {"position": v(-217.18, -65.86) * mm});
            skPoint(sketch, "E159", {"position": v(-217.18, -160.86) * mm});
            skPoint(sketch, "E160", {"position": v(-262.18, -65.86) * mm});
            skPoint(sketch, "E161", {"position": v(-172.18, -65.86) * mm});
            skPoint(sketch, "E162", {"position": v(-307.18, -89.6) * mm});
            skPoint(sketch, "E163", {"position": v(-307.18, -137.1) * mm});
            skPoint(sketch, "E164", {"position": v(-284.68, -65.86) * mm});
            skPoint(sketch, "E165", {"position": v(-239.68, -65.86) * mm});
            skPoint(sketch, "E166", {"position": v(-194.68, -65.86) * mm});
            skPoint(sketch, "E167", {"position": v(-149.68, -65.86) * mm});
            skPoint(sketch, "E168", {"position": v(-284.68, -89.6) * mm});
            skCircle(sketch, "E169", {"center": v(-284.68, -89.6) * mm, "radius": 10 * mm});
            skPoint(sketch, "E170", {"position": v(-262.18, -89.6) * mm});
            skPoint(sketch, "E171", {"position": v(-239.68, -89.6) * mm});
            skPoint(sketch, "E172", {"position": v(-217.18, -89.6) * mm});
            skPoint(sketch, "E173", {"position": v(-194.68, -89.6) * mm});
            skPoint(sketch, "E174", {"position": v(-172.18, -89.6) * mm});
            skPoint(sketch, "E175", {"position": v(-149.68, -89.6) * mm});
            skCircle(sketch, "E176", {"center": v(-262.18, -89.6) * mm, "radius": 10 * mm});
            skCircle(sketch, "E177", {"center": v(-239.68, -89.6) * mm, "radius": 10 * mm});
            skCircle(sketch, "E178", {"center": v(-217.18, -89.6) * mm, "radius": 10 * mm});
            skCircle(sketch, "E179", {"center": v(-194.68, -89.6) * mm, "radius": 10 * mm});
            skCircle(sketch, "E180", {"center": v(-172.18, -89.6) * mm, "radius": 10 * mm});
            skCircle(sketch, "E181", {"center": v(-149.68, -89.6) * mm, "radius": 10 * mm});
            skPoint(sketch, "E182", {"position": v(-284.68, -113.36) * mm});
            skPoint(sketch, "E183", {"position": v(-262.18, -113.36) * mm});
            skPoint(sketch, "E184", {"position": v(-239.68, -113.36) * mm});
            skPoint(sketch, "E185", {"position": v(-194.68, -113.36) * mm});
            skPoint(sketch, "E186", {"position": v(-172.18, -113.36) * mm});
            skPoint(sketch, "E187", {"position": v(-149.68, -137.1) * mm});
            skPoint(sketch, "E188", {"position": v(-172.18, -137.1) * mm});
            skPoint(sketch, "E189", {"position": v(-194.68, -137.1) * mm});
            skPoint(sketch, "E190", {"position": v(-217.18, -137.1) * mm});
            skPoint(sketch, "E191", {"position": v(-239.68, -137.1) * mm});
            skPoint(sketch, "E192", {"position": v(-262.18, -137.1) * mm});
            skPoint(sketch, "E193", {"position": v(-284.68, -137.1) * mm});
            skPoint(sketch, "E194", {"position": v(-149.68, -113.36) * mm});
            skCircle(sketch, "E195", {"center": v(-284.68, -113.36) * mm, "radius": 10 * mm});
            skCircle(sketch, "E196", {"center": v(-262.18, -113.36) * mm, "radius": 10 * mm});
            skCircle(sketch, "E197", {"center": v(-239.68, -113.36) * mm, "radius": 10 * mm});
            skCircle(sketch, "E198", {"center": v(-217.18, -113.36) * mm, "radius": 10 * mm});
            skCircle(sketch, "E199", {"center": v(-194.68, -113.36) * mm, "radius": 10 * mm});
            skCircle(sketch, "E200", {"center": v(-172.18, -113.36) * mm, "radius": 10 * mm});
            skCircle(sketch, "E201", {"center": v(-149.68, -113.36) * mm, "radius": 10 * mm});
            skCircle(sketch, "E202", {"center": v(-149.68, -137.1) * mm, "radius": 10 * mm});
            skCircle(sketch, "E203", {"center": v(-172.18, -137.1) * mm, "radius": 10 * mm});
            skCircle(sketch, "E204", {"center": v(-194.68, -137.1) * mm, "radius": 10 * mm});
            skCircle(sketch, "E205", {"center": v(-217.18, -137.1) * mm, "radius": 10 * mm});
            skCircle(sketch, "E206", {"center": v(-239.68, -137.1) * mm, "radius": 10 * mm});
            skCircle(sketch, "E207", {"center": v(-262.18, -137.1) * mm, "radius": 10 * mm});
            skCircle(sketch, "E208", {"center": v(-284.68, -137.1) * mm, "radius": 10 * mm});
            skSolve(sketch);
        }
        {
            var Q0;
            Q0=makeQuery(id+"F24.imprint","IMPRINT",FACE,{"disambiguationData":[TD([[makeQuery(id+"F24.imprint","IMPRINT",EDGE,{"derivedFrom":sQuery(id+"F24.wireOp",EDGE,"E147.bottom")}),-1.0]])]});
            extrude(context, id + "F25", {"entities" : qUnion([Q0]), "depth" : 2 * mm, "offsetDistance" : 25 * mm});
        }
    });
